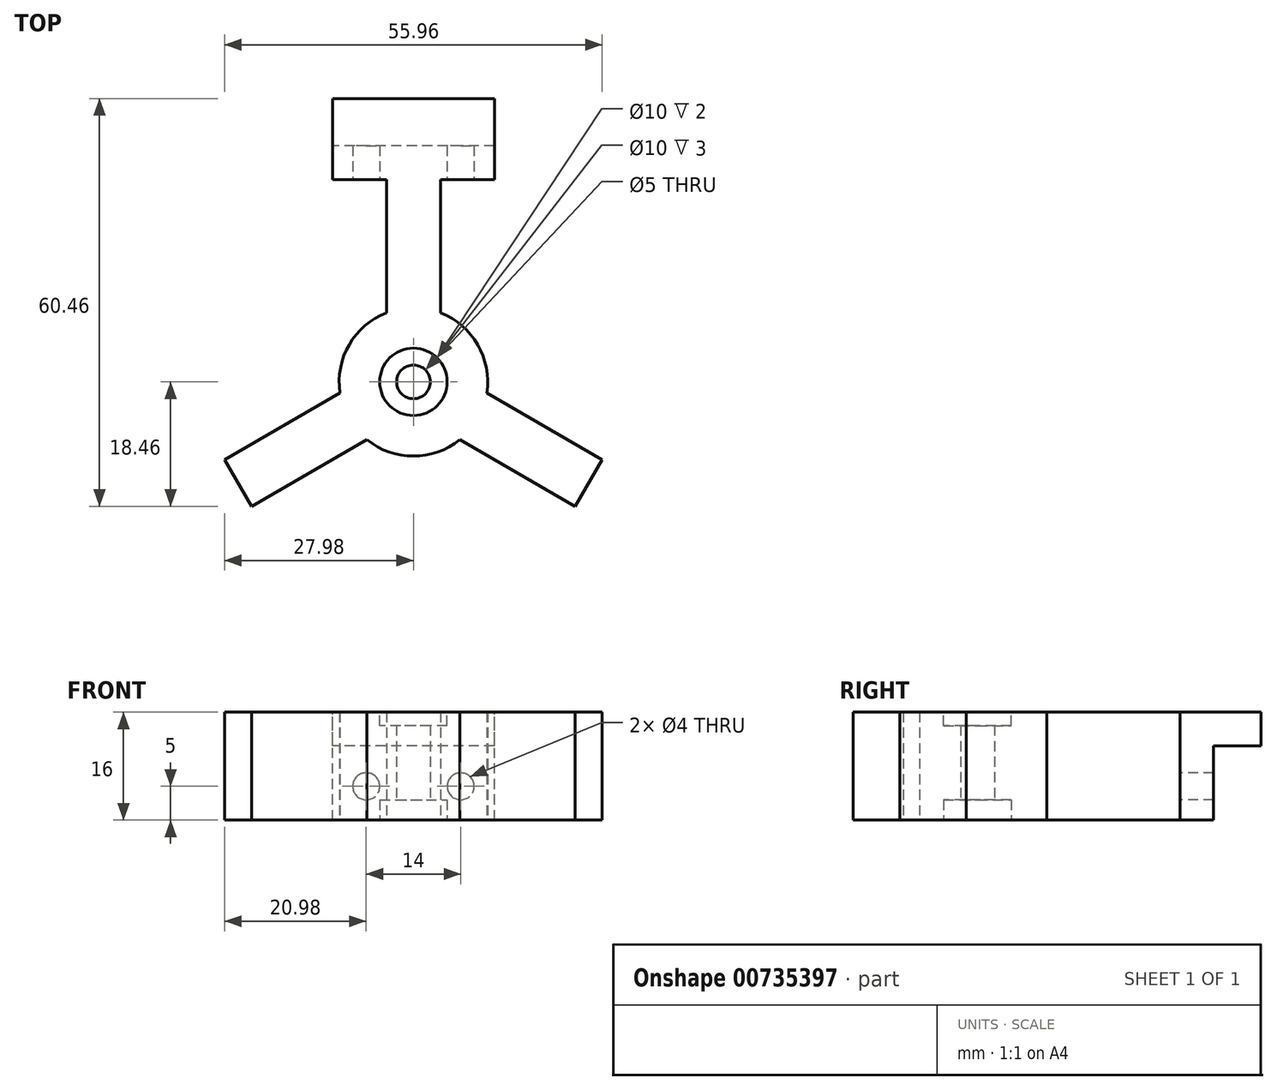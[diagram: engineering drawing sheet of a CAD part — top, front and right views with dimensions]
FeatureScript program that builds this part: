
annotation { "Feature Type Name" : "Feature", "Feature Type Description" : "" }
export const myFeature = defineFeature(function(context is Context, id is Id, definition is map)
    precondition{}
    {
        {
            var Q0;
            Q0=qCreatedBy(makeId("Top.planeOp"),FACE);
            var sketch = newSketch(context, id + "F0", { "sketchPlane" : qUnion([Q0])});
            skArc(sketch, "E0", {"start": v(-6.87, -8.59) * mm, "mid": v(0, -11) * mm, "end": v(6.87, -8.59) * mm});
            skLineSegment(sketch, "E1.bottom", {"start": v(-23.98, -18.46) * mm, "end": v(-27.98, -11.54) * mm});
            skLineSegment(sketch, "E1.left", {"start": v(-23.98, -18.46) * mm, "end": v(-6.87, -8.59) * mm});
            skLineSegment(sketch, "E1.right", {"start": v(-27.98, -11.54) * mm, "end": v(-10.87, -1.66) * mm});
            skLineSegment(sketch, "E2.1.0", {"start": v(23.98, -18.46) * mm, "end": v(6.87, -8.59) * mm});
            skLineSegment(sketch, "E2.1.1", {"start": v(27.98, -11.54) * mm, "end": v(10.87, -1.66) * mm});
            skLineSegment(sketch, "E2.1.2", {"start": v(27.98, -11.54) * mm, "end": v(23.98, -18.46) * mm});
            skLineSegment(sketch, "E2.2.0", {"start": v(4, 30) * mm, "end": v(4, 10.25) * mm});
            skLineSegment(sketch, "E2.2.1", {"start": v(-4, 30) * mm, "end": v(-4, 10.25) * mm});
            skLineSegment(sketch, "E2.2.2", {"start": v(-4, 30) * mm, "end": v(4, 30) * mm});
            skArc(sketch, "E3.trimOffspring", {"start": v(10.87, -1.66) * mm, "mid": v(9.53, 5.5) * mm, "end": v(4, 10.25) * mm});
            skArc(sketch, "E4.trimOffspring", {"start": v(-4, 10.25) * mm, "mid": v(-9.53, 5.5) * mm, "end": v(-10.87, -1.66) * mm});
            skSolve(sketch);
        }
        {
            var Q0;
            Q0 = qSketchRegion(id + "F0", true);
            extrude(context, id + "F1", {"entities" : qUnion([Q0]), "depth" : 16 * mm, "offsetDistance" : 25 * mm});
        }
        {
            var Q0;
            Q0=makeQuery(id+"F1.opExtrude","CAP_FACE",FACE,{"disambiguationData":[OSD([sQuery(id+"F0.wireOp",EDGE,"E0"),sQuery(id+"F0.wireOp",EDGE,"E1.bottom"),sQuery(id+"F0.wireOp",EDGE,"E1.left"),sQuery(id+"F0.wireOp",EDGE,"E1.right"),sQuery(id+"F0.wireOp",EDGE,"E2.1.0"),sQuery(id+"F0.wireOp",EDGE,"E2.1.1"),sQuery(id+"F0.wireOp",EDGE,"E2.1.2"),sQuery(id+"F0.wireOp",EDGE,"E2.2.0"),sQuery(id+"F0.wireOp",EDGE,"E2.2.1"),sQuery(id+"F0.wireOp",EDGE,"E2.2.2"),sQuery(id+"F0.wireOp",EDGE,"E3.trimOffspring"),sQuery(id+"F0.wireOp",EDGE,"E4.trimOffspring")])],"isStart":false});
            var sketch = newSketch(context, id + "F2", { "sketchPlane" : qUnion([Q0])});
            skCircle(sketch, "E5", {"center": v(0, 0) * mm, "radius": 5 * mm});
            skSolve(sketch);
        }
        {
            var Q0;
            Q0=makeQuery(id+"F2.imprint","IMPRINT",FACE,{"disambiguationData":[TD([[makeQuery(id+"F2.imprint","IMPRINT",EDGE,{"derivedFrom":sQuery(id+"F2.wireOp",EDGE,"E5")}),1.0]])]});
            extrude(context, id + "F3", {"entities" : qUnion([Q0]), "operationType" : NewBodyOperationType.REMOVE, "oppositeDirection" : true, "depth" : 2 * mm, "offsetDistance" : 25 * mm});
        }
        {
            var Q0;
            Q0=makeQuery(id+"F1.opExtrude","CAP_FACE",FACE,{"disambiguationData":[OSD([sQuery(id+"F0.wireOp",EDGE,"E0"),sQuery(id+"F0.wireOp",EDGE,"E1.bottom"),sQuery(id+"F0.wireOp",EDGE,"E1.left"),sQuery(id+"F0.wireOp",EDGE,"E1.right"),sQuery(id+"F0.wireOp",EDGE,"E2.1.0"),sQuery(id+"F0.wireOp",EDGE,"E2.1.1"),sQuery(id+"F0.wireOp",EDGE,"E2.1.2"),sQuery(id+"F0.wireOp",EDGE,"E2.2.0"),sQuery(id+"F0.wireOp",EDGE,"E2.2.1"),sQuery(id+"F0.wireOp",EDGE,"E2.2.2"),sQuery(id+"F0.wireOp",EDGE,"E3.trimOffspring"),sQuery(id+"F0.wireOp",EDGE,"E4.trimOffspring")])],"isStart":true});
            var sketch = newSketch(context, id + "F4", { "sketchPlane" : qUnion([Q0])});
            skCircle(sketch, "E6", {"center": v(0, 0) * mm, "radius": 5 * mm});
            skSolve(sketch);
        }
        {
            var Q0;
            Q0=makeQuery(id+"F4.imprint","IMPRINT",FACE,{"disambiguationData":[TD([[makeQuery(id+"F4.imprint","IMPRINT",EDGE,{"derivedFrom":sQuery(id+"F4.wireOp",EDGE,"E6")}),1.0]])]});
            extrude(context, id + "F5", {"entities" : qUnion([Q0]), "operationType" : NewBodyOperationType.REMOVE, "oppositeDirection" : true, "depth" : 3 * mm, "offsetDistance" : 25 * mm});
        }
        {
            var Q0;
            Q0=makeQuery(id+"F5.boolean.opBoolean","COPY",FACE,{"derivedFrom":makeQuery(id+"F5.opExtrude","CAP_FACE",FACE,{"disambiguationData":[OSD([sQuery(id+"F4.wireOp",EDGE,"E6")])],"isStart":false})});
            var sketch = newSketch(context, id + "F6", { "sketchPlane" : qUnion([Q0])});
            skCircle(sketch, "E7", {"center": v(0, 0) * mm, "radius": 2.5 * mm});
            skSolve(sketch);
        }
        {
            var Q0;
            Q0=makeQuery(id+"F6.imprint","IMPRINT",FACE,{"disambiguationData":[TD([[makeQuery(id+"F6.imprint","IMPRINT",EDGE,{"derivedFrom":sQuery(id+"F6.wireOp",EDGE,"E7")}),1.0]])]});
            extrude(context, id + "F7", {"entities" : qUnion([Q0]), "operationType" : NewBodyOperationType.REMOVE, "endBound" : BoundingType.THROUGH_ALL, "oppositeDirection" : true, "depth" : 25 * mm, "offsetDistance" : 25 * mm});
        }
        {
            var Q0;
            Q0=makeQuery(id+"F1.opExtrude","CAP_FACE",FACE,{"disambiguationData":[OSD([sQuery(id+"F0.wireOp",EDGE,"E0"),sQuery(id+"F0.wireOp",EDGE,"E1.bottom"),sQuery(id+"F0.wireOp",EDGE,"E1.left"),sQuery(id+"F0.wireOp",EDGE,"E1.right"),sQuery(id+"F0.wireOp",EDGE,"E2.1.0"),sQuery(id+"F0.wireOp",EDGE,"E2.1.1"),sQuery(id+"F0.wireOp",EDGE,"E2.1.2"),sQuery(id+"F0.wireOp",EDGE,"E2.2.0"),sQuery(id+"F0.wireOp",EDGE,"E2.2.1"),sQuery(id+"F0.wireOp",EDGE,"E2.2.2"),sQuery(id+"F0.wireOp",EDGE,"E3.trimOffspring"),sQuery(id+"F0.wireOp",EDGE,"E4.trimOffspring")])],"isStart":false});
            var sketch = newSketch(context, id + "F8", { "sketchPlane" : qUnion([Q0])});
            skLineSegment(sketch, "E8", {"start": v(-12, 42) * mm, "end": v(-12, 30) * mm});
            skLineSegment(sketch, "E9", {"start": v(-12, 30) * mm, "end": v(12, 30) * mm});
            skLineSegment(sketch, "E10", {"start": v(12, 30) * mm, "end": v(12, 42) * mm});
            skLineSegment(sketch, "E11", {"start": v(12, 42) * mm, "end": v(-12, 42) * mm});
            skPoint(sketch, "E12.center.orphan", {"position": v(0, 0) * mm});
            skSolve(sketch);
        }
        {
            var Q0;
            Q0 = qSketchRegion(id + "F8", true);
            extrude(context, id + "F9", {"entities" : qUnion([Q0]), "operationType" : NewBodyOperationType.ADD, "oppositeDirection" : true, "depth" : 5 * mm, "offsetDistance" : 25 * mm});
        }
        {
            var Q0;
            Q0=makeQuery(id+"F9.opExtrude","CAP_FACE",FACE,{"disambiguationData":[OSD([sQuery(id+"F8.wireOp",EDGE,"E12"),sQuery(id+"F8.wireOp",EDGE,"E8"),sQuery(id+"F8.wireOp",EDGE,"E9"),sQuery(id+"F8.wireOp",EDGE,"E10")])],"isStart":false});
            var sketch = newSketch(context, id + "F10", { "sketchPlane" : qUnion([Q0])});
            skLineSegment(sketch, "E13.bottom", {"start": v(12, -30) * mm, "end": v(-12, -30) * mm});
            skLineSegment(sketch, "E13.top", {"start": v(12, -35) * mm, "end": v(-12, -35) * mm});
            skLineSegment(sketch, "E13.left", {"start": v(12, -30) * mm, "end": v(12, -35) * mm});
            skLineSegment(sketch, "E13.right", {"start": v(-12, -30) * mm, "end": v(-12, -35) * mm});
            skSolve(sketch);
        }
        {
            var Q0;
            Q0=makeQuery(id+"F10.imprint","IMPRINT",FACE,{"disambiguationData":[TD([[makeQuery(id+"F10.imprint","IMPRINT",EDGE,{"derivedFrom":sQuery(id+"F10.wireOp",EDGE,"E13.top")}),-1.0]])]});
            extrude(context, id + "F11", {"entities" : qUnion([Q0]), "operationType" : NewBodyOperationType.ADD, "depth" : 11 * mm, "offsetDistance" : 25 * mm});
        }
        {
            var Q0;
            {var subQ2=sQuery(id+"F0.wireOp",EDGE,"E2.2.1");var subQ5=sQuery(id+"F8.wireOp",EDGE,"E9");Q0=makeQuery(id+"F11.boolean.opBoolean","MERGE",FACE,{"derivedFrom":[makeQuery(id+"F9.boolean.opBoolean","SPLIT",FACE,{"disambiguationData":[TD([makeQuery(id+"F1.opExtrude","SWEPT_FACE",FACE,{"disambiguationData":[OSD([subQ2])]})])],"derivedFrom":makeQuery(id+"F9.opExtrude","SWEPT_FACE",FACE,{"disambiguationData":[OSD([subQ5])]})}),makeQuery(id+"F11.opExtrude","SWEPT_FACE",FACE,{"disambiguationData":[OSD([sQuery(id+"F10.wireOp",EDGE,"E13.bottom")])]})]});}
            var sketch = newSketch(context, id + "F12", { "sketchPlane" : qUnion([Q0])});
            skPoint(sketch, "E14", {"position": v(-7, 5) * mm});
            skPoint(sketch, "E15", {"position": v(7, 5) * mm});
            skSolve(sketch);
        }
        {
            var Q0;
            Q0=sQuery(id+"F12.wireOp",VERTEX,"E15");
            var Q1;
            Q1=sQuery(id+"F12.wireOp",VERTEX,"E14");
            var Q2;
            Q2=makeQuery(id+"F1.opExtrude","SWEPT_BODY",BODY,{"disambiguationData":[OSD([sQuery(id+"F0.wireOp",EDGE,"E0"),sQuery(id+"F0.wireOp",EDGE,"E1.bottom"),sQuery(id+"F0.wireOp",EDGE,"E1.left"),sQuery(id+"F0.wireOp",EDGE,"E1.right"),sQuery(id+"F0.wireOp",EDGE,"E2.1.0"),sQuery(id+"F0.wireOp",EDGE,"E2.1.1"),sQuery(id+"F0.wireOp",EDGE,"E2.1.2"),sQuery(id+"F0.wireOp",EDGE,"E2.2.0"),sQuery(id+"F0.wireOp",EDGE,"E2.2.1"),sQuery(id+"F0.wireOp",EDGE,"E2.2.2"),sQuery(id+"F0.wireOp",EDGE,"E3.trimOffspring"),sQuery(id+"F0.wireOp",EDGE,"E4.trimOffspring")])]});
            hole(context, id + "F13", {"style" : HoleStyle.SIMPLE, "endStyle" : HoleEndStyle.THROUGH, "holeDiameter" : 4 * mm, "majorDiameter" : 5 * mm, "isTappedThrough" : true, "tappedDepth" : 12 * mm, "tapClearance" : 3, "locations" : qUnion([Q0, Q1]), "scope" : qUnion([Q2])});
        }
    });
